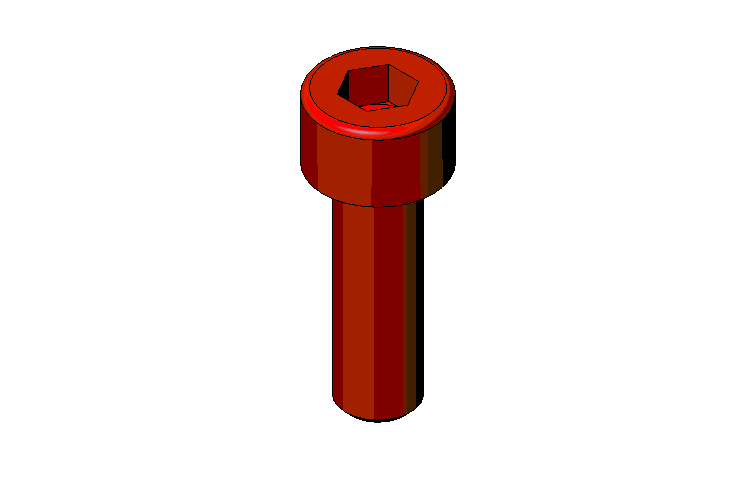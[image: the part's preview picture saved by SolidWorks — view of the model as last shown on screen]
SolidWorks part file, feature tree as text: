
SOLIDWORKS PART (.sldprt)
format: sldprt  version: not decoded by parser v0  size: 220,160 bytes
history: native  units: mm
features: plane x3, sketch x3, material x1, extrude x1, chamfer x1, revolve x1, cut_extrude x1 (+10 scaffold rows collapsed)
feature tree (21):
  scaffold x10  (default folders/planes/origin — collapsed)
  material  "Matériau <non spécifié>"
  plane  "Plan1"
  plane  "Plan2"
  plane  "Plan3"
  sketch  "Esquisse2"  dims[Diamètre nominal=5.0mm]
  extrude  "Base-Extrusion"  Depth=16mm Longueur sous tête=16mm
  chamfer  "Chanfrein1"  Distance=0.5mm Angle=45deg
  sketch  "Esquisse5"  dims[c1.D2=0.5mm c1.Hauteur tête=2.0mm c1.Cote sur plats=5.5mm c1.D3=~2.780036mm c2.D3=30.0deg c2.D4=2.75mm c2.Diamètre tête=8.5mm c2.Diamètre nominal=3.0mm c2.D1=4.25mm c3.D3=3.0mm c4.D3=60.0deg c4.Diamètre nominal=5.0mm c4.Cote sur plats=4.0mm c4.D4=2.5mm c4.D5=2.0mm]
  revolve  "Boss.-Révol.1"  Angle=360deg
  sketch  "Esquisse7"  dims[c1.D1=~2.410714mm c2.D1=30.0deg c2.D2=~1.370242mm c3.D2=30.0deg c3.D3=2.5mm]
  cut_extrude  "Enlèv. mat.-Extru.1"  Depth=2.5mm
decode coverage: 7 of 7 modeling features carry decoded parameters
note: ~ marks probable driven/reference dimensions
note: suppression state not decoded; provenance and decode notes live in map.json
